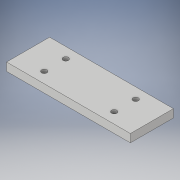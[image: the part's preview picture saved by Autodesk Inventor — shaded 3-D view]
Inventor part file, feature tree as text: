
AUTODESK INVENTOR PART (.ipt)
format: ipt  version: 2019 (Build 230136000, 136)  size: 107,008 bytes
history: native  units: in
note: dims shown in document units (in); Inventor stores cm internally (conversion verified against a paired STEP export)
features: extrude x1, sketch x1
ambient origin geometry x8: Origin, YZ Plane, XZ Plane, XY Plane, X Axis, Y Axis, Z Axis, Center Point
bodies: Solid1 (feature_tree)
feature tree (2):
  extrude  "Extrusion1"  Depth=11.5in
  sketch  "Sketch1"  dims[d0=4.0in d1=11.5in d2=0.5in d3=0.5in d4=0.5in d5=0.5in d6=1.0in d7=2.0in d8=2.5in d9=1.0in d10=2.0in d11=2.5in d12=2.5in d13=2.5in d14=0.75in d15=0.0in]
